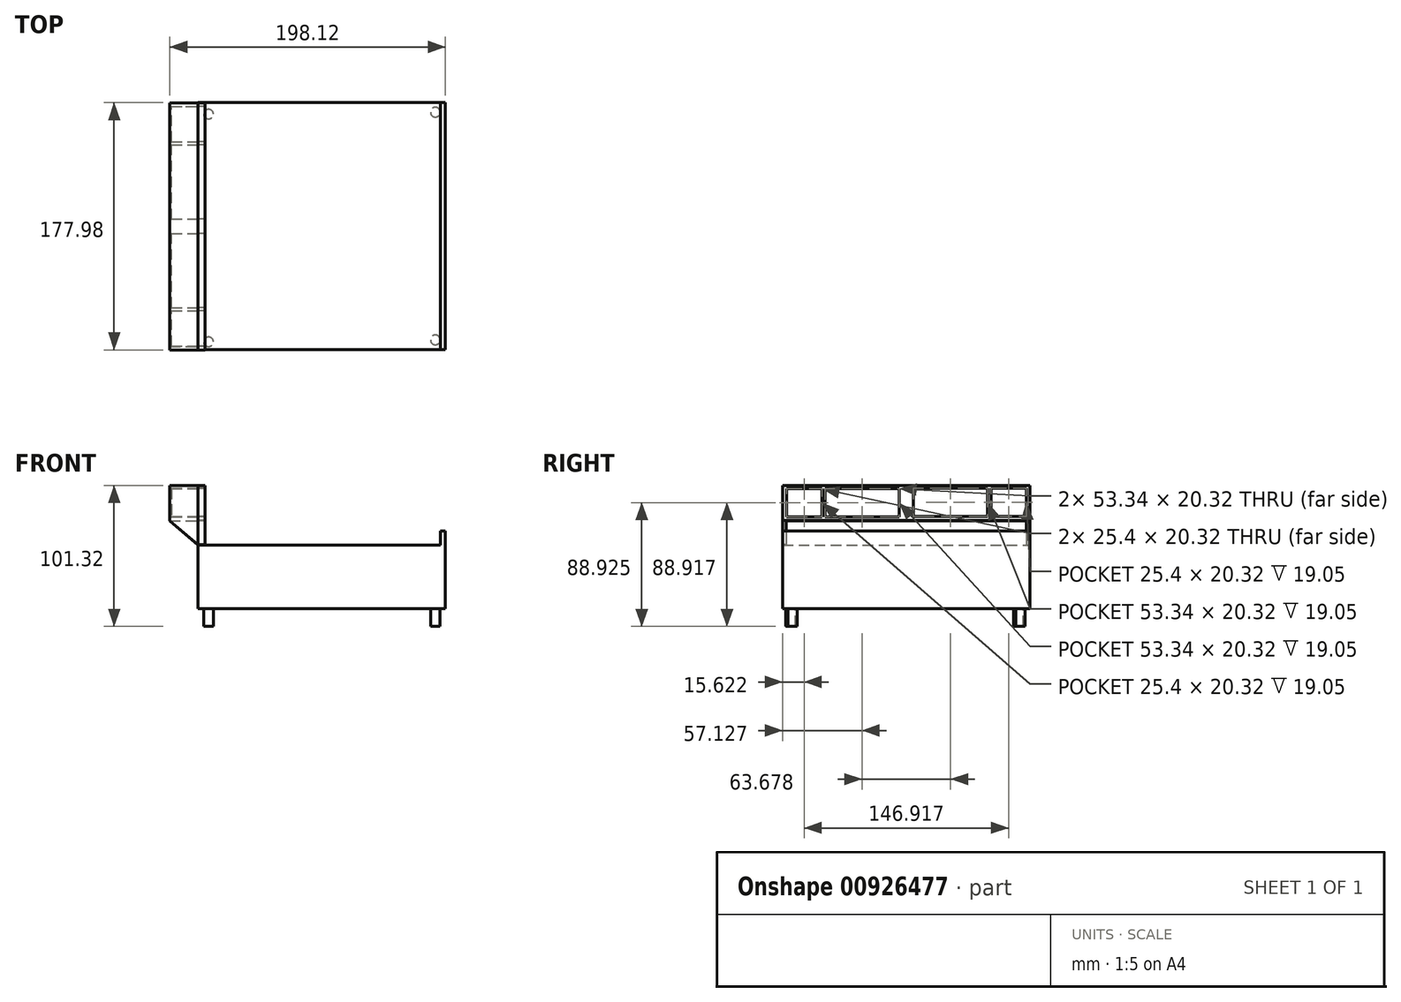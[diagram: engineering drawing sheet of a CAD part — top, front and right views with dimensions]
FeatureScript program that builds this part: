
annotation { "Feature Type Name" : "Feature", "Feature Type Description" : "" }
export const myFeature = defineFeature(function(context is Context, id is Id, definition is map)
    precondition{}
    {
        {
            var Q0;
            Q0=qCreatedBy(makeId("Top.planeOp"),FACE);
            var sketch = newSketch(context, id + "F0", { "sketchPlane" : qUnion([Q0])});
            skLineSegment(sketch, "E0.bottom", {"start": v(88.9, -88.9) * mm, "end": v(-88.9, -88.9) * mm});
            skLineSegment(sketch, "E0.top", {"start": v(88.9, 88.9) * mm, "end": v(-88.9, 88.9) * mm});
            skLineSegment(sketch, "E0.left", {"start": v(88.9, -88.9) * mm, "end": v(88.9, 88.9) * mm});
            skLineSegment(sketch, "E0.right", {"start": v(-88.9, -88.9) * mm, "end": v(-88.9, 88.9) * mm});
            skPoint(sketch, "E0.middle", {"position": v(0, 0) * mm});
            skSolve(sketch);
        }
        {
            var Q0;
            Q0=makeQuery(id+"F0.imprint","IMPRINT",FACE,{"disambiguationData":[TD([[makeQuery(id+"F0.imprint","IMPRINT",EDGE,{"derivedFrom":sQuery(id+"F0.wireOp",EDGE,"E0.bottom")}),-1.0]])]});
            extrude(context, id + "F1", {"entities" : qUnion([Q0]), "depth" : 45.72 * mm, "offsetDistance" : 25.4 * mm});
        }
        {
            var Q0;
            Q0=makeQuery(id+"F1.opExtrude","CAP_FACE",FACE,{"disambiguationData":[OSD([sQuery(id+"F0.wireOp",EDGE,"E0.bottom"),sQuery(id+"F0.wireOp",EDGE,"E0.top"),sQuery(id+"F0.wireOp",EDGE,"E0.left"),sQuery(id+"F0.wireOp",EDGE,"E0.right")])],"isStart":false});
            var sketch = newSketch(context, id + "F2", { "sketchPlane" : qUnion([Q0])});
            skLineSegment(sketch, "E1.bottom", {"start": v(88.9, -88.9) * mm, "end": v(85.47, -88.9) * mm});
            skLineSegment(sketch, "E1.top", {"start": v(88.9, 88.9) * mm, "end": v(85.47, 88.9) * mm});
            skLineSegment(sketch, "E1.left", {"start": v(88.9, -88.9) * mm, "end": v(88.9, 88.9) * mm});
            skLineSegment(sketch, "E1.right", {"start": v(85.47, -88.9) * mm, "end": v(85.47, 88.9) * mm});
            skPoint(sketch, "E1.middle", {"position": v(87.19, 0) * mm});
            skSolve(sketch);
        }
        {
            var Q0;
            Q0=makeQuery(id+"F2.imprint","IMPRINT",FACE,{"disambiguationData":[TD([[makeQuery(id+"F2.imprint","IMPRINT",EDGE,{"derivedFrom":sQuery(id+"F2.wireOp",EDGE,"E1.bottom")}),-1.0]])]});
            extrude(context, id + "F3", {"entities" : qUnion([Q0]), "operationType" : NewBodyOperationType.ADD, "depth" : 10.16 * mm, "offsetDistance" : 25.4 * mm});
        }
        {
            var Q0;
            Q0=makeQuery(id+"F1.opExtrude","SWEPT_FACE",FACE,{"disambiguationData":[OSD([sQuery(id+"F0.wireOp",EDGE,"E0.right")])]});
            var sketch = newSketch(context, id + "F4", { "sketchPlane" : qUnion([Q0])});
            skLineSegment(sketch, "E2.bottom", {"start": v(-88.9, 45.72) * mm, "end": v(88.9, 45.72) * mm});
            skLineSegment(sketch, "E2.top", {"start": v(-88.9, 63.5) * mm, "end": v(88.9, 63.5) * mm});
            skLineSegment(sketch, "E2.left", {"start": v(-88.9, 45.72) * mm, "end": v(-88.9, 63.5) * mm});
            skLineSegment(sketch, "E2.right", {"start": v(88.9, 45.72) * mm, "end": v(88.9, 63.5) * mm});
            skSolve(sketch);
        }
        {
            var Q0;
            Q0=makeQuery(id+"F4.imprint","IMPRINT",FACE,{"disambiguationData":[TD([[makeQuery(id+"F4.imprint","IMPRINT",EDGE,{"derivedFrom":sQuery(id+"F4.wireOp",EDGE,"E2.bottom")}),1.0]])]});
            var sketch = newSketch(context, id + "F5", { "sketchPlane" : qUnion([Q0])});
            skLineSegment(sketch, "E3.bottom", {"start": v(-88.72, 63.22) * mm, "end": v(89.08, 63.22) * mm});
            skLineSegment(sketch, "E3.top", {"start": v(-88.72, 88.62) * mm, "end": v(89.08, 88.62) * mm});
            skLineSegment(sketch, "E3.left", {"start": v(-88.72, 63.22) * mm, "end": v(-88.72, 88.62) * mm});
            skLineSegment(sketch, "E3.right", {"start": v(89.08, 63.22) * mm, "end": v(89.08, 88.62) * mm});
            skSolve(sketch);
        }
        {
            var Q0;
            Q0=makeQuery(id+"F5.imprint","IMPRINT",FACE,{"disambiguationData":[TD([[makeQuery(id+"F5.imprint","IMPRINT",EDGE,{"derivedFrom":sQuery(id+"F5.wireOp",EDGE,"E3.bottom")}),1.0]])]});
            extrude(context, id + "F6", {"entities" : qUnion([Q0]), "depth" : 20.32 * mm, "offsetDistance" : 25.4 * mm});
        }
        {
            var Q0;
            Q0=makeQuery(id+"F6.opExtrude","SWEPT_FACE",FACE,{"disambiguationData":[OSD([sQuery(id+"F5.wireOp",EDGE,"E3.right")])]});
            var sketch = newSketch(context, id + "F7", { "sketchPlane" : qUnion([Q0])});
            skLineSegment(sketch, "E4", {"start": v(-109.22, 63.22) * mm, "end": v(-88.9, 63.22) * mm});
            skLineSegment(sketch, "E5", {"start": v(-88.9, 63.22) * mm, "end": v(-88.9, 46.04) * mm});
            skLineSegment(sketch, "E6", {"start": v(-88.9, 46.04) * mm, "end": v(-109.22, 63.22) * mm});
            skSolve(sketch);
        }
        {
            var Q0;
            Q0=makeQuery(id+"F7.imprint","IMPRINT",FACE,{"disambiguationData":[TD([[makeQuery(id+"F7.imprint","IMPRINT",EDGE,{"derivedFrom":sQuery(id+"F7.wireOp",EDGE,"E4")}),-1.0]])]});
            extrude(context, id + "F8", {"entities" : qUnion([Q0]), "operationType" : NewBodyOperationType.ADD, "oppositeDirection" : true, "depth" : 2.54 * mm, "offsetDistance" : 25.4 * mm});
        }
        {
            var Q0;
            Q0=makeQuery(id+"F6.opExtrude","SWEPT_FACE",FACE,{"disambiguationData":[OSD([sQuery(id+"F5.wireOp",EDGE,"E3.left")])]});
            var sketch = newSketch(context, id + "F9", { "sketchPlane" : qUnion([Q0])});
            skLineSegment(sketch, "E7", {"start": v(109.22, 63.22) * mm, "end": v(88.9, 63.22) * mm});
            skLineSegment(sketch, "E8", {"start": v(88.9, 63.22) * mm, "end": v(88.9, 45.79) * mm});
            skLineSegment(sketch, "E9", {"start": v(88.9, 45.79) * mm, "end": v(109.22, 63.22) * mm});
            skSolve(sketch);
        }
        {
            var Q0;
            Q0=makeQuery(id+"F9.imprint","IMPRINT",FACE,{"disambiguationData":[TD([[makeQuery(id+"F9.imprint","IMPRINT",EDGE,{"derivedFrom":sQuery(id+"F9.wireOp",EDGE,"E7")}),1.0]])]});
            extrude(context, id + "F10", {"entities" : qUnion([Q0]), "operationType" : NewBodyOperationType.ADD, "oppositeDirection" : true, "depth" : 2.54 * mm, "offsetDistance" : 25.4 * mm});
        }
        {
            var Q0;
            Q0=makeQuery(id+"F10.boolean.opBoolean","MERGE",FACE,{"derivedFrom":[makeQuery(id+"F8.boolean.opBoolean","MERGE",FACE,{"derivedFrom":[makeQuery(id+"F6.opExtrude","CAP_FACE",FACE,{"disambiguationData":[OSD([sQuery(id+"F5.wireOp",EDGE,"E3.bottom"),sQuery(id+"F5.wireOp",EDGE,"E3.top"),sQuery(id+"F5.wireOp",EDGE,"E3.left"),sQuery(id+"F5.wireOp",EDGE,"E3.right")])],"isStart":true}),makeQuery(id+"F8.opExtrude","SWEPT_FACE",FACE,{"disambiguationData":[OSD([sQuery(id+"F7.wireOp",EDGE,"E5")])]})]}),makeQuery(id+"F10.opExtrude","SWEPT_FACE",FACE,{"disambiguationData":[OSD([sQuery(id+"F9.wireOp",EDGE,"E8")])]})]});
            var sketch = newSketch(context, id + "F11", { "sketchPlane" : qUnion([Q0])});
            skLineSegment(sketch, "E10.bottom", {"start": v(-86.16, 86.39) * mm, "end": v(-60.76, 86.39) * mm});
            skLineSegment(sketch, "E10.top", {"start": v(-86.16, 66.07) * mm, "end": v(-60.76, 66.07) * mm});
            skLineSegment(sketch, "E10.left", {"start": v(-86.16, 86.39) * mm, "end": v(-86.16, 66.07) * mm});
            skLineSegment(sketch, "E10.right", {"start": v(-60.76, 86.39) * mm, "end": v(-60.76, 66.07) * mm});
            skLineSegment(sketch, "E11.bottom", {"start": v(-58.62, 86.38) * mm, "end": v(-5.28, 86.38) * mm});
            skLineSegment(sketch, "E11.top", {"start": v(-58.62, 66.06) * mm, "end": v(-5.28, 66.06) * mm});
            skLineSegment(sketch, "E11.left", {"start": v(-58.62, 86.38) * mm, "end": v(-58.62, 66.06) * mm});
            skLineSegment(sketch, "E11.right", {"start": v(-5.28, 86.38) * mm, "end": v(-5.28, 66.06) * mm});
            skLineSegment(sketch, "E12.bottom", {"start": v(5.05, 86.58) * mm, "end": v(58.4, 86.58) * mm});
            skLineSegment(sketch, "E12.top", {"start": v(5.05, 66.26) * mm, "end": v(58.4, 66.26) * mm});
            skLineSegment(sketch, "E12.left", {"start": v(5.05, 86.58) * mm, "end": v(5.05, 66.26) * mm});
            skLineSegment(sketch, "E12.right", {"start": v(58.4, 86.58) * mm, "end": v(58.4, 66.26) * mm});
            skLineSegment(sketch, "E13.bottom", {"start": v(60.76, 86.58) * mm, "end": v(86.16, 86.58) * mm});
            skLineSegment(sketch, "E13.top", {"start": v(60.76, 66.26) * mm, "end": v(86.16, 66.26) * mm});
            skLineSegment(sketch, "E13.left", {"start": v(60.76, 86.58) * mm, "end": v(60.76, 66.26) * mm});
            skLineSegment(sketch, "E13.right", {"start": v(86.16, 86.58) * mm, "end": v(86.16, 66.26) * mm});
            skSolve(sketch);
        }
        {
            var Q0;
            Q0=makeQuery(id+"F11.imprint","IMPRINT",FACE,{"disambiguationData":[TD([[makeQuery(id+"F11.imprint","IMPRINT",EDGE,{"derivedFrom":sQuery(id+"F11.wireOp",EDGE,"E10.bottom")}),-1.0]])]});
            var Q1;
            Q1=makeQuery(id+"F11.imprint","IMPRINT",FACE,{"disambiguationData":[TD([[makeQuery(id+"F11.imprint","IMPRINT",EDGE,{"derivedFrom":sQuery(id+"F11.wireOp",EDGE,"E11.bottom")}),-1.0]])]});
            var Q2;
            Q2=makeQuery(id+"F11.imprint","IMPRINT",FACE,{"disambiguationData":[TD([[makeQuery(id+"F11.imprint","IMPRINT",EDGE,{"derivedFrom":sQuery(id+"F11.wireOp",EDGE,"E12.bottom")}),-1.0]])]});
            var Q3;
            Q3=makeQuery(id+"F11.imprint","IMPRINT",FACE,{"disambiguationData":[TD([[makeQuery(id+"F11.imprint","IMPRINT",EDGE,{"derivedFrom":sQuery(id+"F11.wireOp",EDGE,"E13.bottom")}),-1.0]])]});
            extrude(context, id + "F12", {"entities" : qUnion([Q0, Q1, Q2, Q3]), "operationType" : NewBodyOperationType.REMOVE, "oppositeDirection" : true, "depth" : 19.05 * mm, "offsetDistance" : 25.4 * mm});
        }
        {
            var Q0;
            Q0=makeQuery(id+"F10.boolean.opBoolean","MERGE",FACE,{"derivedFrom":[makeQuery(id+"F8.boolean.opBoolean","MERGE",FACE,{"derivedFrom":[makeQuery(id+"F6.opExtrude","CAP_FACE",FACE,{"disambiguationData":[OSD([sQuery(id+"F5.wireOp",EDGE,"E3.bottom"),sQuery(id+"F5.wireOp",EDGE,"E3.top"),sQuery(id+"F5.wireOp",EDGE,"E3.left"),sQuery(id+"F5.wireOp",EDGE,"E3.right")])],"isStart":true}),makeQuery(id+"F8.opExtrude","SWEPT_FACE",FACE,{"disambiguationData":[OSD([sQuery(id+"F7.wireOp",EDGE,"E5")])]})]}),makeQuery(id+"F10.opExtrude","SWEPT_FACE",FACE,{"disambiguationData":[OSD([sQuery(id+"F9.wireOp",EDGE,"E8")])]})]});
            var Q1;
            Q1=makeQuery(id+"F4.imprint","IMPRINT",FACE,{"disambiguationData":[TD([[makeQuery(id+"F4.imprint","IMPRINT",EDGE,{"derivedFrom":sQuery(id+"F4.wireOp",EDGE,"E2.bottom")}),-1.0]])]});
            extrude(context, id + "F13", {"entities" : qUnion([Q0, Q1]), "depth" : 5.08 * mm, "offsetDistance" : 25.4 * mm});
        }
        {
            var Q0;
            Q0=makeQuery(id+"F1.opExtrude","CAP_FACE",FACE,{"disambiguationData":[OSD([sQuery(id+"F0.wireOp",EDGE,"E0.bottom"),sQuery(id+"F0.wireOp",EDGE,"E0.top"),sQuery(id+"F0.wireOp",EDGE,"E0.left"),sQuery(id+"F0.wireOp",EDGE,"E0.right")])],"isStart":true});
            var sketch = newSketch(context, id + "F14", { "sketchPlane" : qUnion([Q0])});
            skCircle(sketch, "E14", {"center": v(-81.4, 83.25) * mm, "radius": 3.48 * mm});
            skCircle(sketch, "E15.0.1.0", {"center": v(-81.4, -80.58) * mm, "radius": 3.48 * mm});
            skCircle(sketch, "E15.1.0.0", {"center": v(81.66, 81.84) * mm, "radius": 3.48 * mm});
            skCircle(sketch, "E15.1.1.0", {"center": v(81.66, -81.99) * mm, "radius": 3.48 * mm});
            skLineSegment(sketch, "E15.direction1", {"start": v(-81.4, 83.25) * mm, "end": v(81.66, 81.84) * mm, "construction": true});
            skLineSegment(sketch, "E15.direction2", {"start": v(-81.4, 83.25) * mm, "end": v(-81.4, -80.58) * mm, "construction": true});
            skSolve(sketch);
        }
        {
            var Q0;
            Q0=makeQuery(id+"F14.imprint","IMPRINT",FACE,{"disambiguationData":[TD([[makeQuery(id+"F14.imprint","IMPRINT",EDGE,{"derivedFrom":sQuery(id+"F14.wireOp",EDGE,"E14")}),1.0]])]});
            var Q1;
            Q1=makeQuery(id+"F14.imprint","IMPRINT",FACE,{"disambiguationData":[TD([[makeQuery(id+"F14.imprint","IMPRINT",EDGE,{"derivedFrom":sQuery(id+"F14.wireOp",EDGE,"E15.1.0.0")}),1.0]])]});
            var Q2;
            Q2=makeQuery(id+"F14.imprint","IMPRINT",FACE,{"disambiguationData":[TD([[makeQuery(id+"F14.imprint","IMPRINT",EDGE,{"derivedFrom":sQuery(id+"F14.wireOp",EDGE,"E15.1.1.0")}),1.0]])]});
            var Q3;
            Q3=makeQuery(id+"F14.imprint","IMPRINT",FACE,{"disambiguationData":[TD([[makeQuery(id+"F14.imprint","IMPRINT",EDGE,{"derivedFrom":sQuery(id+"F14.wireOp",EDGE,"E15.0.1.0")}),1.0]])]});
            extrude(context, id + "F15", {"entities" : qUnion([Q0, Q1, Q2, Q3]), "operationType" : NewBodyOperationType.ADD, "depth" : 12.7 * mm, "offsetDistance" : 25.4 * mm});
        }
    });
